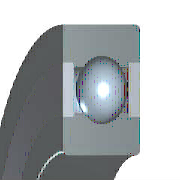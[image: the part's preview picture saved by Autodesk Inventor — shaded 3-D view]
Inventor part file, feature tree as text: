
AUTODESK INVENTOR PART (.ipt)
format: ipt  version: 2017 SP1 (Build 210196100, 196)  size: 307,712 bytes
history: native  units: mm (DEFAULTED — no unit token found)
features: sketch x1, other x1, pattern_circular x1
ambient origin geometry x8: Origin, YZ Plane, XZ Plane, XY Plane, X Axis, Y Axis, Z Axis, Center Point
bodies: Solid1 (feature_tree), Body (feature_tree)
feature tree (3):
  sketch  "Sketch"  dims[d0=3.64mm d17=90.0deg d18=90.0deg d1=0.3mm d2=60.0mm d3=360.0deg d4=0.0mm d5=0.0mm d6=0.0mm d7=8.0mm d8=22.0mm d9=15.0mm d10=22.0mm d11=11.9358mm d12=11.9358mm d13=12.564mm d14=1.166667mm d15=5.833333mm d16=7.0mm d19=1.166667mm d20=2.333333mm d22=3.5mm d23=0.0mm d24=0.0mm]
  other  "Ball"
  pattern_circular  "Balls"  Angle=90.0deg  [1 undecoded]
note: 1 required parameter value undecoded (feature->parameter linkage not recoverable at this tier; creation-order binding heuristic only, values carry confidence <= 0.55)
